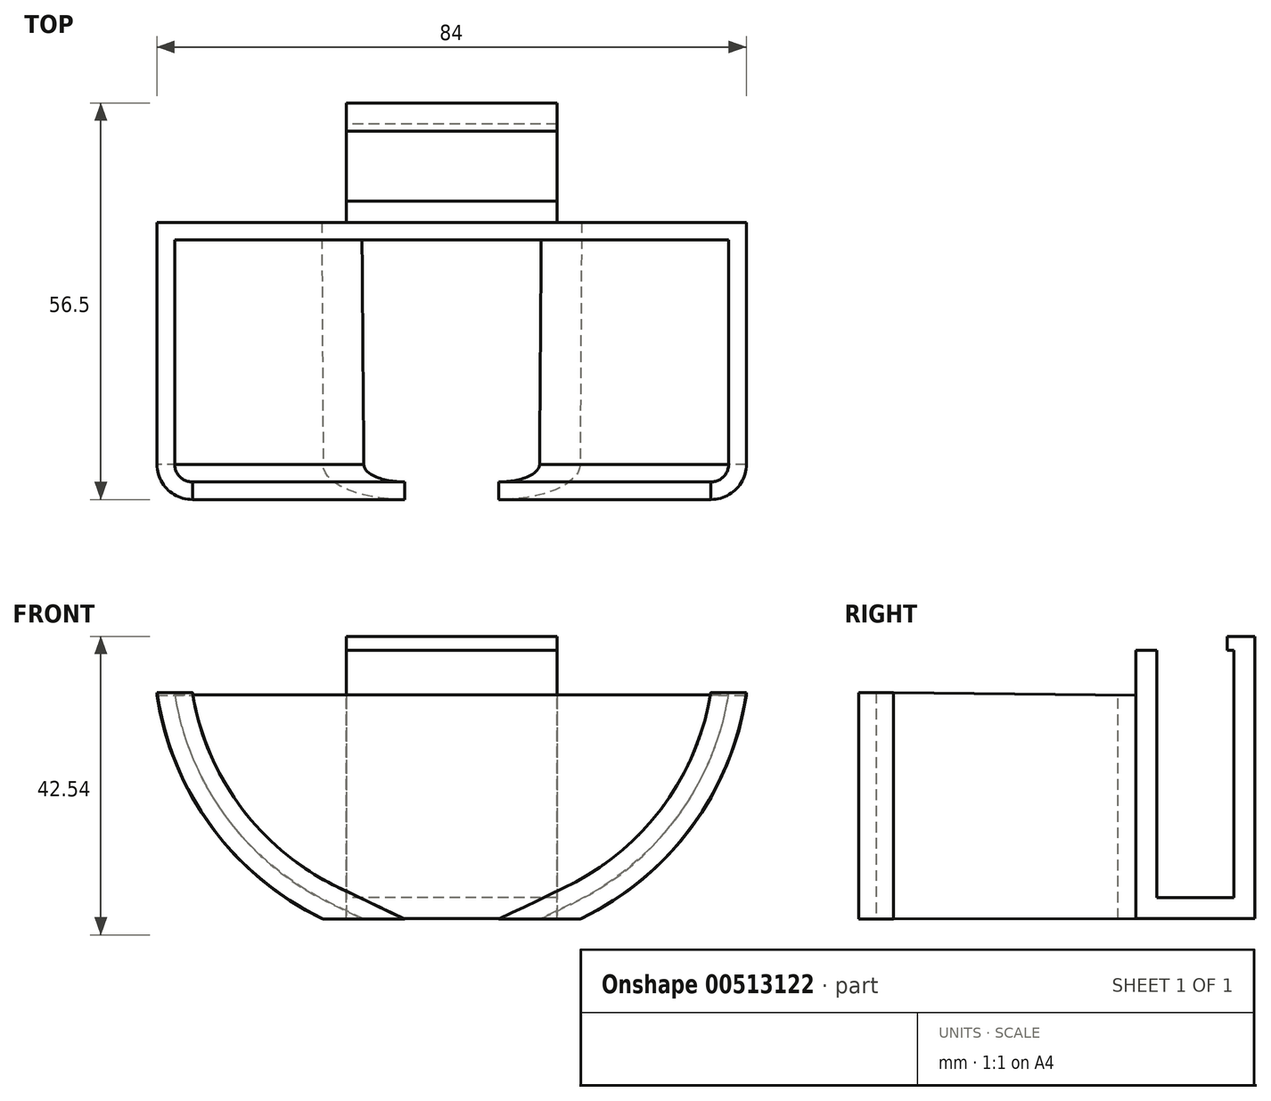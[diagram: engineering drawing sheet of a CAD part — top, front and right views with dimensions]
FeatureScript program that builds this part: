
annotation { "Feature Type Name" : "Feature", "Feature Type Description" : "" }
export const myFeature = defineFeature(function(context is Context, id is Id, definition is map)
    precondition{}
    {
        {
            var Q0;
            Q0=qCreatedBy(makeId("Front.planeOp"),FACE);
            var sketch = newSketch(context, id + "F0", { "sketchPlane" : qUnion([Q0])});
            skCircle(sketch, "E0", {"center": v(0, 0) * mm, "radius": 42.48 * mm});
            skLineSegment(sketch, "E1", {"start": v(-42, -6.38) * mm, "end": v(42, -6.38) * mm});
            skLineSegment(sketch, "E2", {"start": v(-18.52, -38.23) * mm, "end": v(18.52, -38.23) * mm});
            skSolve(sketch);
        }
        {
            var Q0;
            Q0=qCreatedBy(makeId("Right.planeOp"),FACE);
            var sketch = newSketch(context, id + "F1", { "sketchPlane" : qUnion([Q0])});
            skLineSegment(sketch, "E3", {"start": v(0, -38.23) * mm, "end": v(17, -38.23) * mm});
            skLineSegment(sketch, "E4", {"start": v(17, -38.23) * mm, "end": v(17, 0) * mm});
            skLineSegment(sketch, "E5", {"start": v(17, 0) * mm, "end": v(14, 0) * mm});
            skLineSegment(sketch, "E6", {"start": v(14, 0) * mm, "end": v(14, -35.23) * mm});
            skLineSegment(sketch, "E7", {"start": v(14, -35.23) * mm, "end": v(3, -35.23) * mm});
            skLineSegment(sketch, "E8", {"start": v(3, -35.23) * mm, "end": v(3, 0) * mm});
            skLineSegment(sketch, "E9", {"start": v(3, 0) * mm, "end": v(0, 0) * mm});
            skLineSegment(sketch, "E10", {"start": v(0, 0) * mm, "end": v(0, -38.23) * mm});
            skSolve(sketch);
        }
        {
            var Q0;
            Q0=qCreatedBy(makeId("Front.planeOp"),FACE);
            cPlane(context, id + "F2", {"entities" : qUnion([Q0]), "cplaneType" : CPlaneType.OFFSET, "offset" : (32.5 + 7) * mm, "width" : 150 * mm, "height" : 150 * mm});
        }
        {
            var Q0;
            Q0=qCreatedBy(id+"F2.planeOp",FACE);
            var sketch = newSketch(context, id + "F3", { "sketchPlane" : qUnion([Q0])});
            skCircle(sketch, "E11", {"center": v(0, 0) * mm, "radius": 42.43 * mm});
            skLineSegment(sketch, "E12", {"start": v(-42, -6) * mm, "end": v(42, -6) * mm});
            skLineSegment(sketch, "E13", {"start": v(-18.28, -38.29) * mm, "end": v(18.28, -38.29) * mm});
            skSolve(sketch);
        }
        {
            var Q0;
            {var subQ0=sQuery(id+"F0.wireOp",EDGE,"E1");Q0=makeQuery(id+"F0.imprint","IMPRINT",FACE,{"disambiguationData":[TD([[makeQuery(id+"F0.imprint","IMPRINT",EDGE,{"derivedFrom":subQ0}),-1.0]])]});}
            var Q1;
            {var subQ0=sQuery(id+"F3.wireOp",EDGE,"E12");Q1=makeQuery(id+"F3.imprint","IMPRINT",FACE,{"disambiguationData":[TD([[makeQuery(id+"F3.imprint","IMPRINT",EDGE,{"derivedFrom":subQ0}),-1.0]])]});}
            loft(context, id + "F4", {"sheetProfilesArray" : [{ "sheetProfileEntities" : qUnion([Q0]) }, { "sheetProfileEntities" : qUnion([Q1]) }]});
        }
        {
            var Q0;
            {var subQ0=sQuery(id+"F3.wireOp",EDGE,"E12");var subQ1=sQuery(id+"F3.wireOp",EDGE,"E11");var subQ2=makeQuery(id+"F3.imprint","INTERSECT",VERTEX,{"disambiguationData":[OD(0.0)],"derivedFrom":[subQ1,subQ0]});var subQ3=sQuery(id+"F3.wireOp",EDGE,"E13");var subQ4=makeQuery(id+"F3.imprint","INTERSECT",VERTEX,{"disambiguationData":[OD(0.0)],"derivedFrom":[subQ1,subQ3]});Q0=makeQuery(id+"F4.opLoft","MID_CAP_EDGE",EDGE,{"disambiguationData":[OSD([subQ1,subQ0,subQ3]),TDD([subQ2,subQ4,makeQuery(id+"F3.imprint","IMPRINT",EDGE,{"disambiguationData":[TD([[subQ2,-1.0]])],"derivedFrom":subQ1})])],"capPos":1.0});}
            var Q1;
            {var subQ0=sQuery(id+"F3.wireOp",EDGE,"E12");var subQ1=sQuery(id+"F3.wireOp",EDGE,"E11");var subQ2=makeQuery(id+"F3.imprint","INTERSECT",VERTEX,{"disambiguationData":[OD(1.0)],"derivedFrom":[subQ1,subQ0]});var subQ3=sQuery(id+"F3.wireOp",EDGE,"E13");var subQ4=makeQuery(id+"F3.imprint","INTERSECT",VERTEX,{"disambiguationData":[OD(1.0)],"derivedFrom":[subQ1,subQ3]});Q1=makeQuery(id+"F4.opLoft","MID_CAP_EDGE",EDGE,{"disambiguationData":[OSD([subQ1,subQ0,subQ3]),TDD([subQ2,subQ4,makeQuery(id+"F3.imprint","IMPRINT",EDGE,{"disambiguationData":[TD([[subQ2,1.0]])],"derivedFrom":subQ1})])],"capPos":1.0});}
            fillet(context, id + "F5", {"entities" : qUnion([Q0, Q1]), "radius" : 5 * mm, "tangentPropagation" : true, "allowEdgeOverflow" : false});
        }
        {
            var Q0;
            {var subQ0=sQuery(id+"F3.wireOp",EDGE,"E12");Q0=makeQuery(id+"F4.opLoft","CAP_FACE",FACE,{"disambiguationData":[OSD([makeQuery(id+"F3.imprint","IMPRINT",FACE,{"disambiguationData":[TD([[makeQuery(id+"F3.imprint","IMPRINT",EDGE,{"derivedFrom":subQ0}),-1.0]])]})])],"isStart":true});}
            var Q1;
            Q1=makeQuery(id+"F4.opLoft","SWEPT_FACE",FACE,{"disambiguationData":[OSD([sQuery(id+"F0.wireOp",EDGE,"E0"),sQuery(id+"F0.wireOp",EDGE,"E1"),sQuery(id+"F3.wireOp",EDGE,"E11"),sQuery(id+"F3.wireOp",EDGE,"E12")])]});
            var Q2;
            Q2=makeQuery(id+"F4.opLoft","SWEPT_FACE",FACE,{"disambiguationData":[OSD([sQuery(id+"F0.wireOp",EDGE,"E0"),sQuery(id+"F0.wireOp",EDGE,"E2"),sQuery(id+"F3.wireOp",EDGE,"E11"),sQuery(id+"F3.wireOp",EDGE,"E13")])]});
            shell(context, id + "F6", {"entities" : qUnion([Q0, Q1, Q2]), "thickness" : 2.5 * mm});
        }
        {
            var Q0;
            Q0=makeQuery(id+"F1.imprint","IMPRINT",FACE,{"disambiguationData":[TD([[makeQuery(id+"F1.imprint","IMPRINT",EDGE,{"derivedFrom":sQuery(id+"F1.wireOp",EDGE,"E3")}),1.0]])]});
            extrude(context, id + "F7", {"entities" : qUnion([Q0]), "operationType" : NewBodyOperationType.ADD, "depth" : 15 * mm, "offsetDistance" : 25 * mm});
        }
        {
            var Q0;
            Q0=makeQuery(id+"F1.imprint","IMPRINT",FACE,{"disambiguationData":[TD([[makeQuery(id+"F1.imprint","IMPRINT",EDGE,{"derivedFrom":sQuery(id+"F1.wireOp",EDGE,"E3")}),1.0]])]});
            extrude(context, id + "F8", {"entities" : qUnion([Q0]), "operationType" : NewBodyOperationType.ADD, "oppositeDirection" : true, "depth" : 15 * mm, "offsetDistance" : 25 * mm});
        }
        {
            var Q0;
            Q0=qCreatedBy(makeId("Top.planeOp"),FACE);
            var sketch = newSketch(context, id + "F9", { "sketchPlane" : qUnion([Q0])});
            skLineSegment(sketch, "E14.bottom", {"start": v(-15, 13) * mm, "end": v(15, 13) * mm});
            skLineSegment(sketch, "E14.top", {"start": v(-15, 17) * mm, "end": v(15, 17) * mm});
            skLineSegment(sketch, "E14.left", {"start": v(-15, 13) * mm, "end": v(-15, 17) * mm});
            skLineSegment(sketch, "E14.right", {"start": v(15, 13) * mm, "end": v(15, 17) * mm});
            skSolve(sketch);
        }
        {
            var Q0;
            Q0 = qSketchRegion(id + "F9", true);
            extrude(context, id + "F10", {"entities" : qUnion([Q0]), "operationType" : NewBodyOperationType.ADD, "depth" : 2 * mm, "offsetDistance" : 25 * mm});
        }
    });
